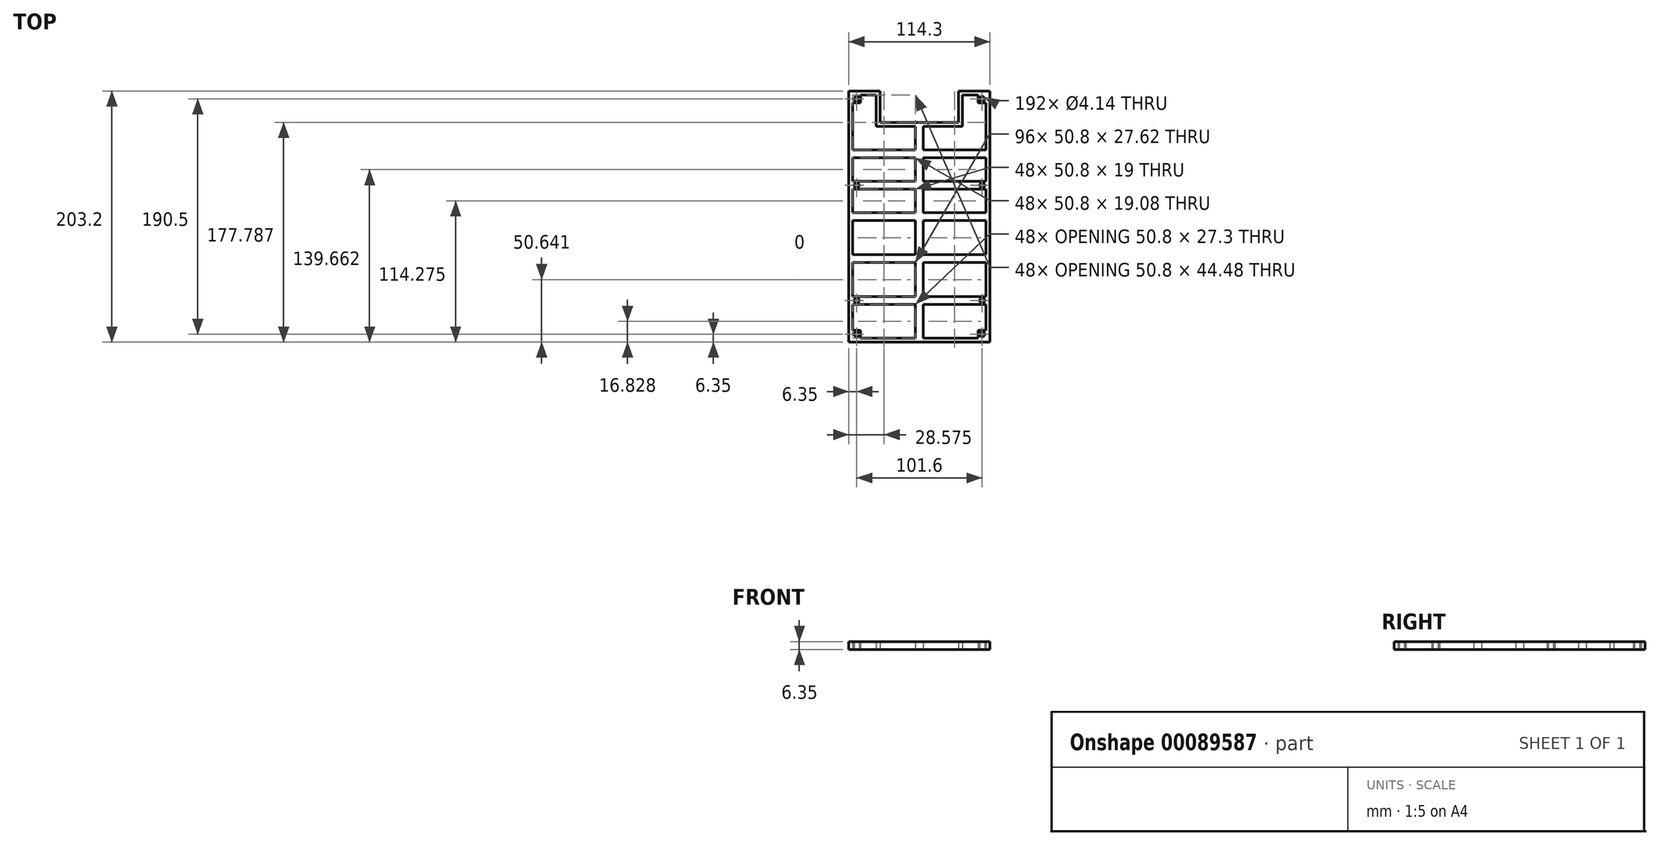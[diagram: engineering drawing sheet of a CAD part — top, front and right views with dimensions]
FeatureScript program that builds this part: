
annotation { "Feature Type Name" : "Feature", "Feature Type Description" : "" }
export const myFeature = defineFeature(function(context is Context, id is Id, definition is map)
    precondition{}
    {
        {
            var Q0;
            Q0=qCreatedBy(makeId("Top.planeOp"),FACE);
            var sketch = newSketch(context, id + "F0", { "sketchPlane" : qUnion([Q0])});
            skLineSegment(sketch, "E0", {"start": v(0, 76.2) * mm, "end": v(-31.75, 76.2) * mm});
            skLineSegment(sketch, "E1", {"start": v(-31.75, 76.2) * mm, "end": v(-31.75, 101.6) * mm});
            skLineSegment(sketch, "E2", {"start": v(-31.75, 101.6) * mm, "end": v(-57.15, 101.6) * mm});
            skLineSegment(sketch, "E3", {"start": v(-57.15, 101.6) * mm, "end": v(-57.15, -101.6) * mm});
            skLineSegment(sketch, "E4", {"start": v(-57.15, -101.6) * mm, "end": v(0, -101.6) * mm});
            skPoint(sketch, "E5", {"position": v(-57.15, 0) * mm});
            skLineSegment(sketch, "E6.0", {"start": v(-47.63, -98.43) * mm, "end": v(-3.17, -98.43) * mm});
            skLineSegment(sketch, "E6.1", {"start": v(-3.18, 73.02) * mm, "end": v(-34.92, 73.02) * mm});
            skLineSegment(sketch, "E6.2", {"start": v(-34.92, 73.02) * mm, "end": v(-34.92, 98.43) * mm});
            skLineSegment(sketch, "E6.3", {"start": v(-34.92, 98.43) * mm, "end": v(-47.63, 98.43) * mm});
            skLineSegment(sketch, "E6.4", {"start": v(-53.98, 92.08) * mm, "end": v(-53.98, 28.52) * mm});
            skLineSegment(sketch, "E7.top", {"start": v(-53.98, 92.08) * mm, "end": v(-47.63, 92.08) * mm});
            skLineSegment(sketch, "E7.right", {"start": v(-47.63, 98.43) * mm, "end": v(-47.63, 92.08) * mm});
            skLineSegment(sketch, "E8.MirrorCS", {"start": v(-53.98, -92.08) * mm, "end": v(-47.63, -92.08) * mm});
            skLineSegment(sketch, "E9.MirrorCS", {"start": v(-47.63, -98.43) * mm, "end": v(-47.63, -92.08) * mm});
            skLineSegment(sketch, "E10", {"start": v(-50.8, 92.08) * mm, "end": v(-50.8, 95.25) * mm, "construction": true});
            skLineSegment(sketch, "E11", {"start": v(-47.63, 95.25) * mm, "end": v(-50.8, 95.25) * mm, "construction": true});
            skLineSegment(sketch, "E12.MirrorCS", {"start": v(-47.63, -95.25) * mm, "end": v(-50.8, -95.25) * mm, "construction": true});
            skLineSegment(sketch, "E13.MirrorCS", {"start": v(-50.8, -92.08) * mm, "end": v(-50.8, -95.25) * mm, "construction": true});
            skCircle(sketch, "E14", {"center": v(-50.8, 95.25) * mm, "radius": 2.07 * mm});
            skCircle(sketch, "E15.MirrorC", {"center": v(-50.8, -95.25) * mm, "radius": 2.07 * mm});
            skLineSegment(sketch, "E16.bottom", {"start": v(-53.98, 28.52) * mm, "end": v(-47.63, 28.52) * mm});
            skLineSegment(sketch, "E16.top", {"start": v(-53.98, 22.17) * mm, "end": v(-47.63, 22.17) * mm});
            skLineSegment(sketch, "E16.right", {"start": v(-47.62, 28.52) * mm, "end": v(-47.62, 22.17) * mm, "construction": true});
            skLineSegment(sketch, "E17", {"start": v(-47.62, 25.35) * mm, "end": v(-50.8, 25.35) * mm, "construction": true});
            skLineSegment(sketch, "E18", {"start": v(-50.8, 25.35) * mm, "end": v(-50.8, 22.17) * mm, "construction": true});
            skCircle(sketch, "E19", {"center": v(-50.8, 25.35) * mm, "radius": 2.07 * mm});
            skLineSegment(sketch, "E20.bottom", {"start": v(-53.98, -64.77) * mm, "end": v(-47.62, -64.77) * mm});
            skLineSegment(sketch, "E20.top", {"start": v(-53.98, -71.12) * mm, "end": v(-47.62, -71.12) * mm});
            skLineSegment(sketch, "E20.right", {"start": v(-47.63, -64.77) * mm, "end": v(-47.63, -71.12) * mm, "construction": true});
            skLineSegment(sketch, "E21", {"start": v(-47.63, -67.95) * mm, "end": v(-50.8, -67.95) * mm, "construction": true});
            skLineSegment(sketch, "E22", {"start": v(-50.8, -67.95) * mm, "end": v(-50.8, -71.12) * mm, "construction": true});
            skCircle(sketch, "E23", {"center": v(-50.8, -67.95) * mm, "radius": 2.07 * mm});
            skLineSegment(sketch, "E24.trimOffspring", {"start": v(-53.98, -71.12) * mm, "end": v(-53.98, -92.08) * mm});
            skLineSegment(sketch, "E25.trimOffspring", {"start": v(-53.98, 22.17) * mm, "end": v(-53.98, 3.17) * mm});
            skLineSegment(sketch, "E26", {"start": v(-53.98, 28.52) * mm, "end": v(-53.98, 22.17) * mm, "construction": true});
            skLineSegment(sketch, "E27.MirrorCS", {"start": v(3.18, 73.02) * mm, "end": v(34.92, 73.02) * mm});
            skLineSegment(sketch, "E28.MirrorCS", {"start": v(0, 76.2) * mm, "end": v(31.75, 76.2) * mm});
            skLineSegment(sketch, "E29.MirrorCS", {"start": v(34.92, 73.02) * mm, "end": v(34.92, 98.43) * mm});
            skLineSegment(sketch, "E30.MirrorCS", {"start": v(31.75, 76.2) * mm, "end": v(31.75, 101.6) * mm});
            skLineSegment(sketch, "E31.MirrorCS", {"start": v(31.75, 101.6) * mm, "end": v(57.15, 101.6) * mm});
            skLineSegment(sketch, "E32.MirrorCS", {"start": v(34.92, 98.43) * mm, "end": v(47.63, 98.43) * mm});
            skLineSegment(sketch, "E33.MirrorCS", {"start": v(47.63, 98.43) * mm, "end": v(47.63, 92.08) * mm});
            skLineSegment(sketch, "E34.MirrorCS", {"start": v(47.63, 95.25) * mm, "end": v(50.8, 95.25) * mm, "construction": true});
            skCircle(sketch, "E35.MirrorC", {"center": v(50.8, 95.25) * mm, "radius": 2.07 * mm});
            skLineSegment(sketch, "E36.MirrorCS", {"start": v(53.98, 92.08) * mm, "end": v(47.63, 92.08) * mm});
            skLineSegment(sketch, "E37.MirrorCS", {"start": v(57.15, 101.6) * mm, "end": v(57.15, -101.6) * mm});
            skLineSegment(sketch, "E38.MirrorCS", {"start": v(53.98, 92.07) * mm, "end": v(53.98, 28.52) * mm});
            skLineSegment(sketch, "E39.MirrorCS", {"start": v(53.98, 28.52) * mm, "end": v(53.98, 22.17) * mm, "construction": true});
            skLineSegment(sketch, "E40.MirrorCS", {"start": v(53.98, 28.52) * mm, "end": v(47.63, 28.52) * mm});
            skCircle(sketch, "E41.MirrorC", {"center": v(50.8, 25.35) * mm, "radius": 2.07 * mm});
            skLineSegment(sketch, "E42.MirrorCS", {"start": v(50.8, 25.35) * mm, "end": v(50.8, 22.17) * mm, "construction": true});
            skLineSegment(sketch, "E43.MirrorCS", {"start": v(53.98, 22.17) * mm, "end": v(47.63, 22.17) * mm});
            skLineSegment(sketch, "E44.MirrorCS", {"start": v(47.62, 28.52) * mm, "end": v(47.62, 22.17) * mm, "construction": true});
            skLineSegment(sketch, "E45.MirrorCS", {"start": v(53.98, 22.17) * mm, "end": v(53.98, 3.18) * mm});
            skLineSegment(sketch, "E46.MirrorCS", {"start": v(53.98, -64.77) * mm, "end": v(47.63, -64.77) * mm});
            skLineSegment(sketch, "E47.MirrorCS", {"start": v(47.62, -64.77) * mm, "end": v(47.62, -71.12) * mm, "construction": true});
            skLineSegment(sketch, "E48.MirrorCS", {"start": v(47.63, -67.95) * mm, "end": v(50.8, -67.95) * mm, "construction": true});
            skLineSegment(sketch, "E49.MirrorCS", {"start": v(50.8, -67.95) * mm, "end": v(50.8, -71.12) * mm, "construction": true});
            skCircle(sketch, "E50.MirrorC", {"center": v(50.8, -67.95) * mm, "radius": 2.07 * mm});
            skLineSegment(sketch, "E51.MirrorCS", {"start": v(53.98, -71.12) * mm, "end": v(47.62, -71.12) * mm});
            skLineSegment(sketch, "E52.MirrorCS", {"start": v(53.98, -71.12) * mm, "end": v(53.98, -92.08) * mm});
            skLineSegment(sketch, "E53.MirrorCS", {"start": v(47.63, -98.43) * mm, "end": v(3.17, -98.43) * mm});
            skLineSegment(sketch, "E54.MirrorCS", {"start": v(57.15, -101.6) * mm, "end": v(0, -101.6) * mm});
            skLineSegment(sketch, "E55.MirrorCS", {"start": v(53.98, -92.08) * mm, "end": v(47.63, -92.08) * mm});
            skLineSegment(sketch, "E56.MirrorCS", {"start": v(47.63, -98.43) * mm, "end": v(47.63, -92.08) * mm});
            skCircle(sketch, "E57.MirrorC", {"center": v(50.8, -95.25) * mm, "radius": 2.07 * mm});
            skLineSegment(sketch, "E58", {"start": v(47.63, 28.52) * mm, "end": v(3.18, 28.52) * mm});
            skLineSegment(sketch, "E59", {"start": v(-47.63, 22.17) * mm, "end": v(-3.18, 22.17) * mm});
            skLineSegment(sketch, "E60", {"start": v(-47.62, -64.77) * mm, "end": v(-3.17, -64.77) * mm});
            skLineSegment(sketch, "E61", {"start": v(47.62, -71.12) * mm, "end": v(3.17, -71.12) * mm});
            skPoint(sketch, "E62", {"position": v(-53.98, 0) * mm});
            skLineSegment(sketch, "E63", {"start": v(-53.98, 3.18) * mm, "end": v(53.98, 3.18) * mm});
            skLineSegment(sketch, "E64.MirrorCS", {"start": v(-53.98, -3.18) * mm, "end": v(53.98, -3.18) * mm});
            skLineSegment(sketch, "E65", {"start": v(-53.98, -3.18) * mm, "end": v(-53.98, -64.77) * mm, "construction": true});
            skPoint(sketch, "E66", {"position": v(-53.98, -33.97) * mm});
            skLineSegment(sketch, "E67", {"start": v(-53.98, -33.97) * mm, "end": v(53.98, -33.97) * mm, "construction": true});
            skLineSegment(sketch, "E68", {"start": v(-53.98, -30.8) * mm, "end": v(-3.17, -30.8) * mm});
            skLineSegment(sketch, "E69.MirrorCS", {"start": v(-53.98, -37.15) * mm, "end": v(-3.17, -37.15) * mm});
            skLineSegment(sketch, "E70", {"start": v(-3.17, -98.43) * mm, "end": v(-3.17, -71.12) * mm});
            skLineSegment(sketch, "E71.MirrorCS", {"start": v(3.17, -98.43) * mm, "end": v(3.17, -71.12) * mm});
            skLineSegment(sketch, "E72.trimOffspring", {"start": v(-3.18, 28.52) * mm, "end": v(-47.63, 28.52) * mm});
            skLineSegment(sketch, "E73.trimOffspring", {"start": v(-3.18, 28.52) * mm, "end": v(-3.18, 47.6) * mm});
            skLineSegment(sketch, "E74.trimOffspring", {"start": v(3.18, 22.17) * mm, "end": v(47.63, 22.17) * mm});
            skLineSegment(sketch, "E75.trimOffspring", {"start": v(3.18, 28.52) * mm, "end": v(3.18, 47.6) * mm});
            skLineSegment(sketch, "E76.trimOffspring", {"start": v(-3.18, 3.18) * mm, "end": v(-3.18, 22.17) * mm});
            skLineSegment(sketch, "E77.trimOffspring", {"start": v(3.18, 3.18) * mm, "end": v(3.18, 22.17) * mm});
            skLineSegment(sketch, "E78.trimOffspring", {"start": v(-53.98, -3.18) * mm, "end": v(-53.98, -64.77) * mm});
            skPoint(sketch, "E79.orphan", {"position": v(0, 73.02) * mm});
            skLineSegment(sketch, "E80.trimOffspring", {"start": v(3.17, -30.8) * mm, "end": v(53.98, -30.8) * mm});
            skLineSegment(sketch, "E81.trimOffspring", {"start": v(-3.17, -30.8) * mm, "end": v(-3.18, -3.18) * mm});
            skLineSegment(sketch, "E82.trimOffspring", {"start": v(3.17, -30.8) * mm, "end": v(3.18, -3.18) * mm});
            skLineSegment(sketch, "E83", {"start": v(-3.17, -64.77) * mm, "end": v(-3.17, -37.15) * mm});
            skLineSegment(sketch, "E84.trimOffspring", {"start": v(3.17, -37.15) * mm, "end": v(53.98, -37.15) * mm});
            skLineSegment(sketch, "E85.trimOffspring", {"start": v(3.17, -64.77) * mm, "end": v(47.62, -64.77) * mm});
            skLineSegment(sketch, "E86.trimOffspring", {"start": v(-3.17, -71.12) * mm, "end": v(-47.62, -71.12) * mm});
            skLineSegment(sketch, "E87.trimOffspring", {"start": v(3.17, -64.77) * mm, "end": v(3.17, -37.15) * mm});
            skLineSegment(sketch, "E88.trimOffspring", {"start": v(53.98, -37.15) * mm, "end": v(53.98, -64.77) * mm});
            skLineSegment(sketch, "E89.trimOffspring", {"start": v(53.98, -3.18) * mm, "end": v(53.98, -30.8) * mm});
            skPoint(sketch, "E90.orphan", {"position": v(0, -98.43) * mm});
            skPoint(sketch, "E91", {"position": v(-3.18, 50.77) * mm});
            skLineSegment(sketch, "E92", {"start": v(-3.18, 50.77) * mm, "end": v(-53.98, 50.77) * mm, "construction": true});
            skLineSegment(sketch, "E93", {"start": v(-53.98, 53.95) * mm, "end": v(-3.18, 53.95) * mm});
            skLineSegment(sketch, "E94.MirrorCS", {"start": v(-53.98, 47.6) * mm, "end": v(-3.18, 47.6) * mm});
            skLineSegment(sketch, "E95.MirrorCS", {"start": v(53.98, 53.95) * mm, "end": v(3.18, 53.95) * mm});
            skLineSegment(sketch, "E96.MirrorCS", {"start": v(53.98, 47.6) * mm, "end": v(3.18, 47.6) * mm});
            skLineSegment(sketch, "E97.trimOffspring", {"start": v(-3.18, 53.95) * mm, "end": v(-3.18, 73.02) * mm});
            skLineSegment(sketch, "E98.trimOffspring", {"start": v(3.18, 53.95) * mm, "end": v(3.18, 73.02) * mm});
            skSolve(sketch);
        }
        {
            var Q0;
            Q0 = qSketchRegion(id + "F0", true);
            extrude(context, id + "F1", {"entities" : qUnion([Q0]), "depth" : 6.35 * mm});
        }
    });
